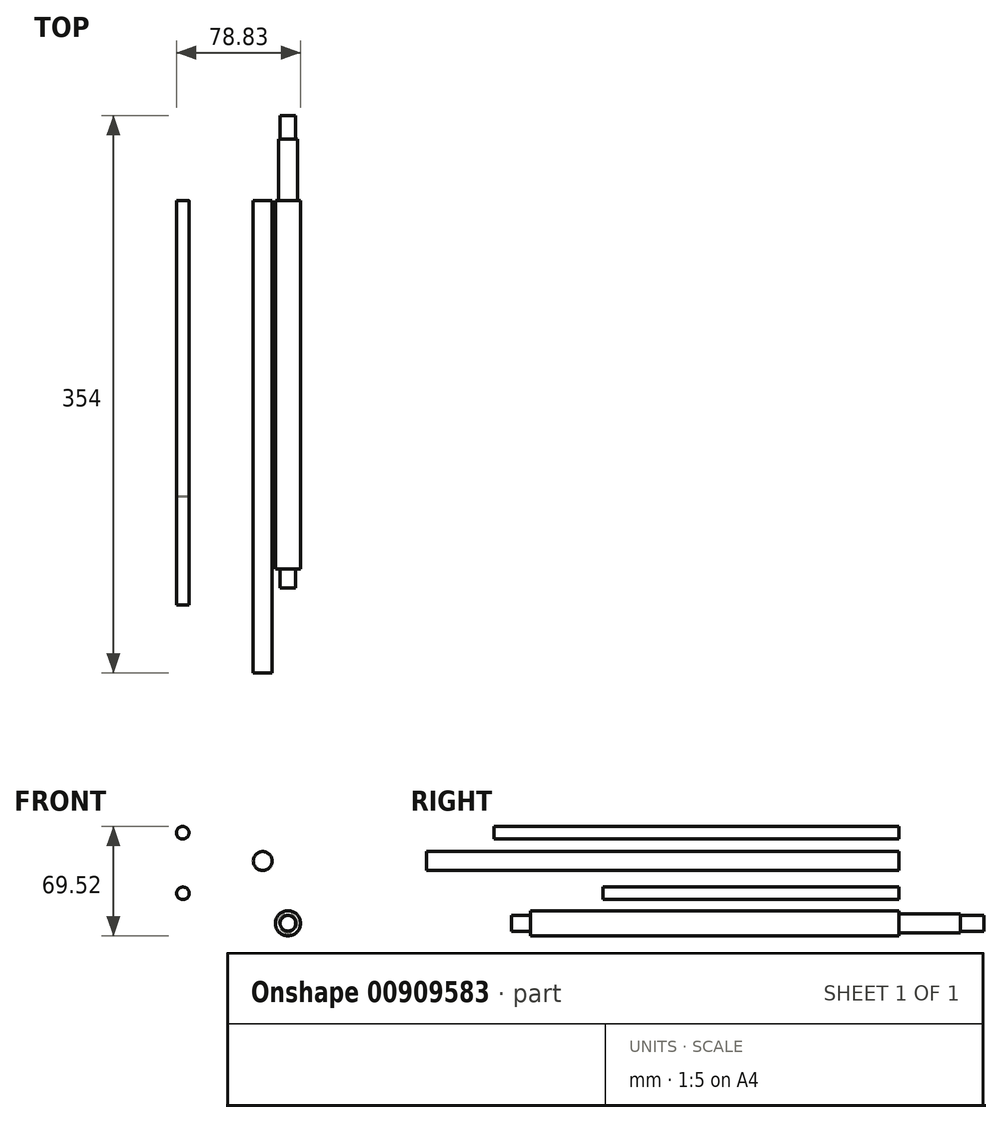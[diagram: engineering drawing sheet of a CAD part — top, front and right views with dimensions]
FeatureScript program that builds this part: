
annotation { "Feature Type Name" : "Feature", "Feature Type Description" : "" }
export const myFeature = defineFeature(function(context is Context, id is Id, definition is map)
    precondition{}
    {
        {
            var Q0;
            Q0=qCreatedBy(makeId("Front.planeOp"),FACE);
            var sketch = newSketch(context, id + "F0", { "sketchPlane" : qUnion([Q0])});
            skCircle(sketch, "E0", {"center": v(-61.71, 42.56) * mm, "radius": 4 * mm});
            skCircle(sketch, "E1", {"center": v(-61.57, 4.07) * mm, "radius": 4 * mm});
            skCircle(sketch, "E2", {"center": v(-10.87, 24.6) * mm, "radius": 6 * mm});
            skCircle(sketch, "E3", {"center": v(5.12, -14.96) * mm, "radius": 8 * mm});
            skSolve(sketch);
        }
        {
            var Q0;
            Q0=makeQuery(id+"F0.imprint","IMPRINT",FACE,{"disambiguationData":[TD([[makeQuery(id+"F0.imprint","IMPRINT",EDGE,{"derivedFrom":sQuery(id+"F0.wireOp",EDGE,"E0")}),1.0]])]});
            extrude(context, id + "F1", {"entities" : qUnion([Q0]), "depth" : 256.97 * mm, "offsetDistance" : 25.4 * mm});
        }
        {
            var Q0;
            Q0=makeQuery(id+"F0.imprint","IMPRINT",FACE,{"disambiguationData":[TD([[makeQuery(id+"F0.imprint","IMPRINT",EDGE,{"derivedFrom":sQuery(id+"F0.wireOp",EDGE,"E1")}),1.0]])]});
            extrude(context, id + "F2", {"entities" : qUnion([Q0]), "depth" : 187.96 * mm, "offsetDistance" : 25.4 * mm});
        }
        {
            var Q0;
            Q0=makeQuery(id+"F0.imprint","IMPRINT",FACE,{"disambiguationData":[TD([[makeQuery(id+"F0.imprint","IMPRINT",EDGE,{"derivedFrom":sQuery(id+"F0.wireOp",EDGE,"E2")}),1.0]])]});
            extrude(context, id + "F3", {"entities" : qUnion([Q0]), "depth" : 300 * mm, "offsetDistance" : 25.4 * mm});
        }
        {
            var Q0;
            Q0=makeQuery(id+"F0.imprint","IMPRINT",FACE,{"disambiguationData":[TD([[makeQuery(id+"F0.imprint","IMPRINT",EDGE,{"derivedFrom":sQuery(id+"F0.wireOp",EDGE,"E3")}),1.0]])]});
            extrude(context, id + "F4", {"entities" : qUnion([Q0]), "depth" : 246 * mm, "offsetDistance" : 25.4 * mm});
        }
        {
            var Q0;
            Q0=makeQuery(id+"F4.opExtrude","CAP_FACE",FACE,{"disambiguationData":[OSD([sQuery(id+"F0.wireOp",EDGE,"E3")])],"isStart":false});
            var sketch = newSketch(context, id + "F5", { "sketchPlane" : qUnion([Q0])});
            skCircle(sketch, "E4", {"center": v(5.12, -14.96) * mm, "radius": 5 * mm});
            skCircle(sketch, "E5", {"center": v(5.12, -14.96) * mm, "radius": 8 * mm});
            skSolve(sketch);
        }
        {
            var Q0;
            Q0=makeQuery(id+"F5.imprint","IMPRINT",FACE,{"disambiguationData":[TD([[makeQuery(id+"F5.imprint","IMPRINT",EDGE,{"derivedFrom":sQuery(id+"F5.wireOp",EDGE,"E4")}),-1.0]])]});
            extrude(context, id + "F6", {"entities" : qUnion([Q0]), "operationType" : NewBodyOperationType.REMOVE, "oppositeDirection" : true, "depth" : 12 * mm, "offsetDistance" : 25.4 * mm});
        }
        {
            var Q0;
            Q0=makeQuery(id+"F0.imprint","IMPRINT",FACE,{"disambiguationData":[TD([[makeQuery(id+"F0.imprint","IMPRINT",EDGE,{"derivedFrom":sQuery(id+"F0.wireOp",EDGE,"E3")}),1.0]])]});
            var sketch = newSketch(context, id + "F7", { "sketchPlane" : qUnion([Q0])});
            skCircle(sketch, "E6", {"center": v(5.12, -14.96) * mm, "radius": 6 * mm});
            skCircle(sketch, "E7", {"center": v(5.12, -14.96) * mm, "radius": 8 * mm});
            skSolve(sketch);
        }
        {
            var Q0;
            Q0=makeQuery(id+"F7.imprint","IMPRINT",FACE,{"disambiguationData":[TD([[makeQuery(id+"F7.imprint","IMPRINT",EDGE,{"derivedFrom":sQuery(id+"F7.wireOp",EDGE,"E6")}),1.0]])]});
            extrude(context, id + "F8", {"entities" : qUnion([Q0]), "operationType" : NewBodyOperationType.ADD, "oppositeDirection" : true, "depth" : 39 * mm, "offsetDistance" : 25.4 * mm});
        }
        {
            var Q0;
            Q0=makeQuery(id+"F8.opExtrude","CAP_FACE",FACE,{"disambiguationData":[OSD([sQuery(id+"F7.wireOp",EDGE,"E6")])],"isStart":false});
            var sketch = newSketch(context, id + "F9", { "sketchPlane" : qUnion([Q0])});
            skCircle(sketch, "E8", {"center": v(-5.12, -14.96) * mm, "radius": 5 * mm});
            skSolve(sketch);
        }
        {
            var Q0;
            Q0=qSketchRegion(id+"F9",true);
            extrude(context, id + "F10", {"entities" : qUnion([Q0]), "operationType" : NewBodyOperationType.ADD, "depth" : 15 * mm, "offsetDistance" : 25.4 * mm});
        }
    });
